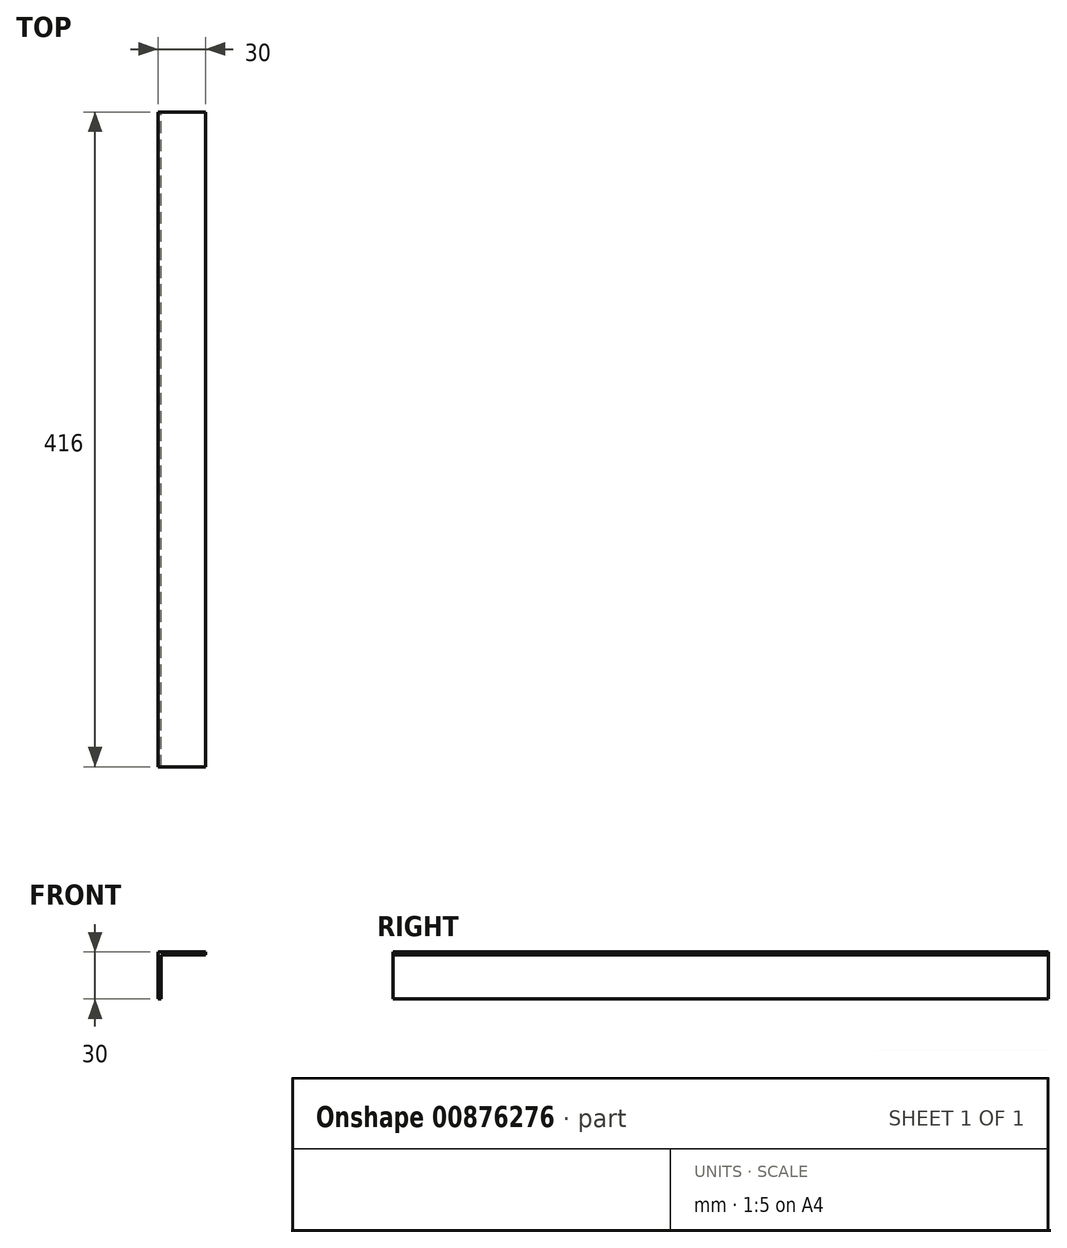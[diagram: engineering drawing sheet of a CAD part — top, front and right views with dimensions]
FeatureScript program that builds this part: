
annotation { "Feature Type Name" : "Feature", "Feature Type Description" : "" }
export const myFeature = defineFeature(function(context is Context, id is Id, definition is map)
    precondition{}
    {
        {
            var Q0;
            Q0=qCreatedBy(makeId("Front.planeOp"),FACE);
            var sketch = newSketch(context, id + "F0", { "sketchPlane" : qUnion([Q0])});
            skLineSegment(sketch, "E0", {"start": v(0, 0) * mm, "end": v(0, 30) * mm});
            skLineSegment(sketch, "E1", {"start": v(0, 30) * mm, "end": v(30, 30) * mm});
            skLineSegment(sketch, "E2.0", {"start": v(2, 28) * mm, "end": v(30, 28) * mm});
            skLineSegment(sketch, "E2.1", {"start": v(2, 0) * mm, "end": v(2, 28) * mm});
            skLineSegment(sketch, "E3", {"start": v(30, 30) * mm, "end": v(30, 28) * mm});
            skLineSegment(sketch, "E4", {"start": v(0, 0) * mm, "end": v(2, 0) * mm});
            skSolve(sketch);
        }
        {
            var Q0;
            Q0=makeQuery(id+"F0.imprint","IMPRINT",FACE,{"disambiguationData":[TD([[makeQuery(id+"F0.imprint","IMPRINT",EDGE,{"derivedFrom":sQuery(id+"F0.wireOp",EDGE,"E0")}),-1.0]])]});
            extrude(context, id + "F1", {"entities" : qUnion([Q0]), "depth" : 496 * mm - 80 * mm, "offsetDistance" : 25.4 * mm});
        }
    });
